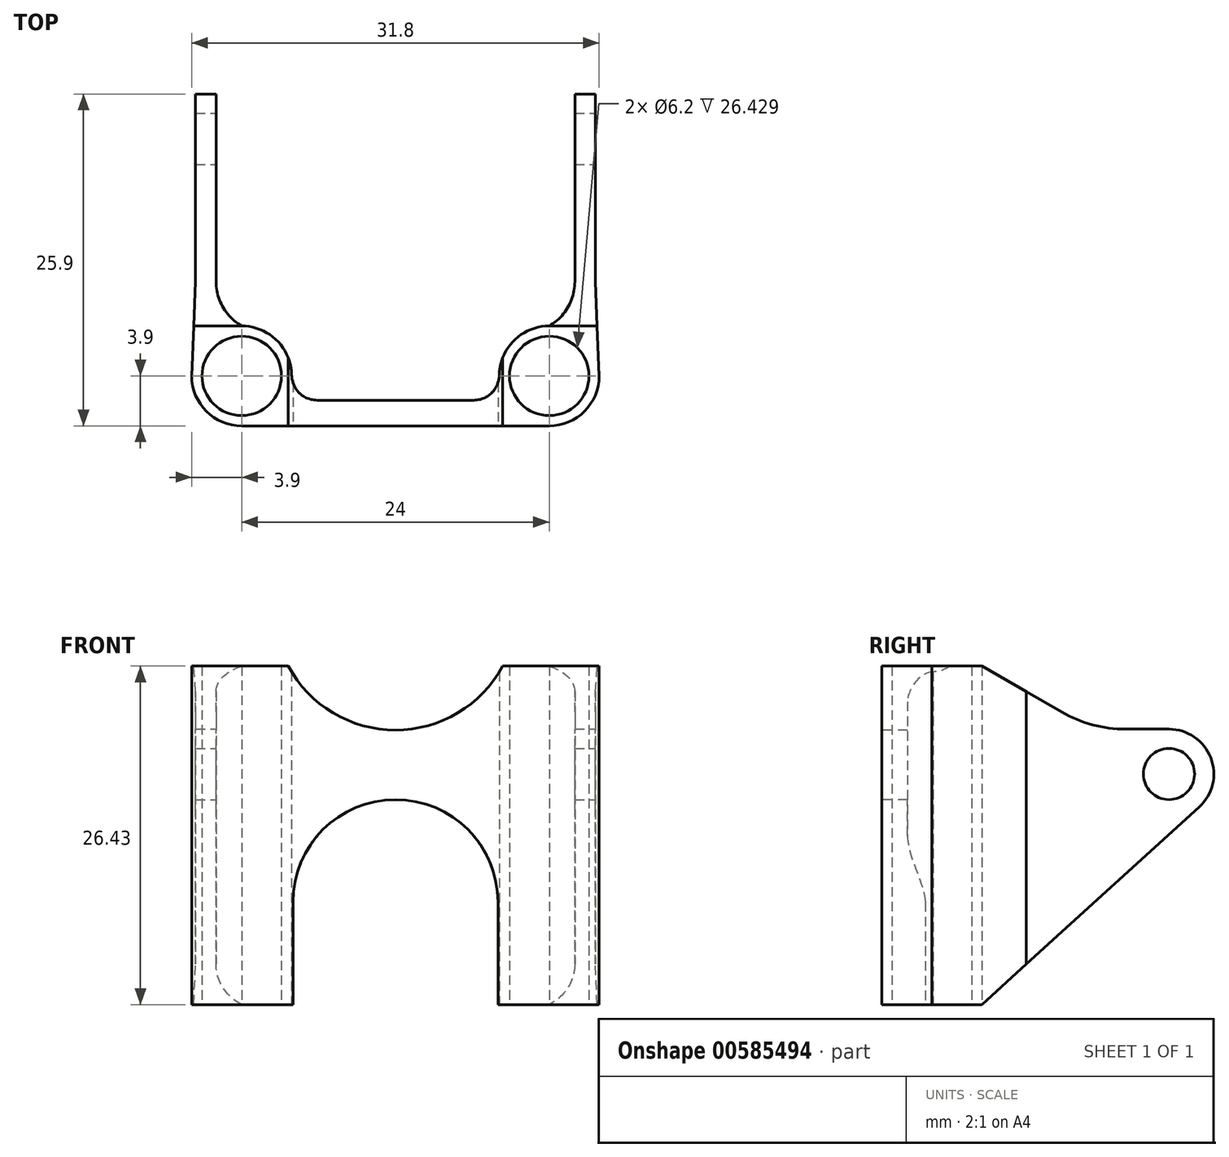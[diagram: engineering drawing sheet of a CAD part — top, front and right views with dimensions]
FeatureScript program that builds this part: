
annotation { "Feature Type Name" : "Feature", "Feature Type Description" : "" }
export const myFeature = defineFeature(function(context is Context, id is Id, definition is map)
    precondition{}
    {
        {
            var Q0;
            Q0=qCreatedBy(makeId("Top.planeOp"),FACE);
            var sketch = newSketch(context, id + "F0", { "sketchPlane" : qUnion([Q0])});
            skCircle(sketch, "E0", {"center": v(-24, 0) * mm, "radius": 3.1 * mm});
            skCircle(sketch, "E1", {"center": v(0, 0) * mm, "radius": 3.1 * mm});
            skLineSegment(sketch, "E2", {"start": v(3.6, 22) * mm, "end": v(2, 22) * mm});
            skLineSegment(sketch, "E3", {"start": v(2, 22) * mm, "end": v(2, 7.36) * mm});
            skLineSegment(sketch, "E4", {"start": v(-27.6, 22) * mm, "end": v(-26, 22) * mm});
            skLineSegment(sketch, "E5", {"start": v(-26, 22) * mm, "end": v(-26, 7.36) * mm});
            skArc(sketch, "E6.filletArc", {"start": v(-26, 7.36) * mm, "mid": v(-25.46, 5.36) * mm, "end": v(-24, 3.9) * mm});
            skArc(sketch, "E7.filletArc", {"start": v(0, 3.9) * mm, "mid": v(1.46, 5.36) * mm, "end": v(2, 7.36) * mm});
            skLineSegment(sketch, "E8", {"start": v(3.6, 22) * mm, "end": v(3.6, 7.36) * mm});
            skCircle(sketch, "E9", {"center": v(0, 0) * mm, "radius": 3.9 * mm});
            skPoint(sketch, "E10.startSnap0", {"position": v(1.46, 5.36) * mm});
            skCircle(sketch, "E11", {"center": v(-24, 0) * mm, "radius": 3.9 * mm});
            skLineSegment(sketch, "E12", {"start": v(-27.6, 22) * mm, "end": v(-27.6, 7.36) * mm});
            skLineSegment(sketch, "E13", {"start": v(0, 0) * mm, "end": v(3.9, 0) * mm, "construction": true});
            skLineSegment(sketch, "E14", {"start": v(-24, 0) * mm, "end": v(-24, 3.9) * mm, "construction": true});
            skLineSegment(sketch, "E15", {"start": v(0, 0) * mm, "end": v(0, 3.9) * mm, "construction": true});
            skLineSegment(sketch, "E16", {"start": v(-24, 0) * mm, "end": v(-27.9, 0) * mm, "construction": true});
            skLineSegment(sketch, "E17", {"start": v(-24, 0) * mm, "end": v(-24, -3.9) * mm, "construction": true});
            skLineSegment(sketch, "E18", {"start": v(0, 0) * mm, "end": v(0, -3.9) * mm, "construction": true});
            skLineSegment(sketch, "E19", {"start": v(0, -3.9) * mm, "end": v(-24, -3.9) * mm});
            skPoint(sketch, "E20", {"position": v(-12, -3.9) * mm});
            skLineSegment(sketch, "E21", {"start": v(-5.9, -1.9) * mm, "end": v(-18.1, -1.9) * mm});
            skLineSegment(sketch, "E22", {"start": v(3.6, 7.36) * mm, "end": v(3.9, 0) * mm});
            skLineSegment(sketch, "E23", {"start": v(-27.6, 7.36) * mm, "end": v(-27.9, 0) * mm});
            skLineSegment(sketch, "E24", {"start": v(0, 0) * mm, "end": v(-3.9, 0) * mm, "construction": true});
            skLineSegment(sketch, "E25", {"start": v(-24, 0) * mm, "end": v(-20.1, 0) * mm, "construction": true});
            skLineSegment(sketch, "E26", {"start": v(-20.1, 0.1) * mm, "end": v(-20.1, 0) * mm});
            skLineSegment(sketch, "E27", {"start": v(-3.9, 0.1) * mm, "end": v(-3.9, 0) * mm});
            skArc(sketch, "E28.filletArc", {"start": v(-5.9, -1.9) * mm, "mid": v(-4.49, -1.31) * mm, "end": v(-3.9, 0.1) * mm});
            skArc(sketch, "E29.filletArc", {"start": v(-20.1, 0.1) * mm, "mid": v(-19.51, -1.31) * mm, "end": v(-18.1, -1.9) * mm});
            skSolve(sketch);
        }
        {
            var Q0;
            Q0=makeQuery(id+"F0.imprint","IMPRINT",FACE,{"disambiguationData":[TD([[makeQuery(id+"F0.imprint","IMPRINT",EDGE,{"derivedFrom":sQuery(id+"F0.wireOp",EDGE,"E0")}),-1.0]])]});
            var Q1;
            Q1=makeQuery(id+"F0.imprint","IMPRINT",FACE,{"disambiguationData":[TD([[makeQuery(id+"F0.imprint","IMPRINT",EDGE,{"derivedFrom":sQuery(id+"F0.wireOp",EDGE,"E4")}),-1.0]])]});
            var Q2;
            {var subQ0=sQuery(id+"F0.wireOp",EDGE,"E19");Q2=makeQuery(id+"F0.imprint","IMPRINT",FACE,{"disambiguationData":[TD([[makeQuery(id+"F0.imprint","IMPRINT",EDGE,{"derivedFrom":subQ0}),-1.0]])]});}
            var Q3;
            Q3=makeQuery(id+"F0.imprint","IMPRINT",FACE,{"disambiguationData":[TD([[makeQuery(id+"F0.imprint","IMPRINT",EDGE,{"derivedFrom":sQuery(id+"F0.wireOp",EDGE,"E1")}),-1.0]])]});
            var Q4;
            Q4=makeQuery(id+"F0.imprint","IMPRINT",FACE,{"disambiguationData":[TD([[makeQuery(id+"F0.imprint","IMPRINT",EDGE,{"derivedFrom":sQuery(id+"F0.wireOp",EDGE,"E2")}),1.0]])]});
            extrude(context, id + "F1", {"entities" : qUnion([Q0, Q1, Q2, Q3, Q4]), "depth" : 35 * mm, "offsetDistance" : 25 * mm});
        }
        {
            var Q0;
            Q0=makeQuery(id+"F1.opExtrude","SWEPT_FACE",FACE,{"disambiguationData":[OSD([sQuery(id+"F0.wireOp",EDGE,"E8")])]});
            var sketch = newSketch(context, id + "F2", { "sketchPlane" : qUnion([Q0])});
            skPoint(sketch, "E30", {"position": v(18.5, 18) * mm});
            skCircle(sketch, "E31", {"center": v(18.5, 18) * mm, "radius": 2 * mm});
            skCircle(sketch, "E32", {"center": v(18.5, 18) * mm, "radius": 3.5 * mm});
            skLineSegment(sketch, "E33", {"start": v(18.5, 18) * mm, "end": v(-11.95, 18) * mm, "construction": true});
            skLineSegment(sketch, "E34", {"start": v(18.5, 18) * mm, "end": v(-7.48, 33) * mm, "construction": true});
            skPoint(sketch, "E35", {"position": v(-7.48, 33) * mm});
            skLineSegment(sketch, "E36", {"start": v(18.5, 21.5) * mm, "end": v(15.12, 21.5) * mm});
            skLineSegment(sketch, "E37", {"start": v(10.12, 22.84) * mm, "end": v(-4.4, 31.22) * mm});
            skPoint(sketch, "E38.visualSharp", {"position": v(12.44, 21.5) * mm});
            skArc(sketch, "E38.filletArc", {"start": v(10.12, 22.84) * mm, "mid": v(12.53, 21.84) * mm, "end": v(15.12, 21.5) * mm});
            skLineSegment(sketch, "E39", {"start": v(-4.4, 31.22) * mm, "end": v(-4.4, 42.85) * mm});
            skLineSegment(sketch, "E40", {"start": v(-4.4, 42.85) * mm, "end": v(29.67, 42.85) * mm});
            skLineSegment(sketch, "E41", {"start": v(29.67, 42.85) * mm, "end": v(29.67, 18) * mm});
            skLineSegment(sketch, "E42", {"start": v(18.5, 18) * mm, "end": v(22, 18) * mm, "construction": true});
            skLineSegment(sketch, "E43", {"start": v(29.67, 18) * mm, "end": v(22, 18) * mm});
            skPoint(sketch, "E44", {"position": v(3.9, 0) * mm});
            skLineSegment(sketch, "E45", {"start": v(3.9, 0) * mm, "end": v(20.85, 15.4) * mm});
            skLineSegment(sketch, "E46", {"start": v(3.9, 0) * mm, "end": v(22, 0) * mm});
            skSolve(sketch);
        }
        {
            var Q0;
            {var subQ6=sQuery(id+"F2.wireOp",EDGE,"E36");Q0=makeQuery(id+"F2.imprint","IMPRINT",FACE,{"disambiguationData":[TD([[makeQuery(id+"F2.imprint","IMPRINT",EDGE,{"derivedFrom":subQ6}),-1.0]])]});}
            var Q1;
            {var subQ0=sQuery(id+"F2.wireOp",EDGE,"E39");Q1=makeQuery(id+"F2.imprint","IMPRINT",FACE,{"disambiguationData":[TD([[makeQuery(id+"F2.imprint","IMPRINT",EDGE,{"derivedFrom":subQ0}),-1.0]])]});}
            var Q2;
            Q2=makeQuery(id+"F2.imprint","IMPRINT",FACE,{"disambiguationData":[TD([[makeQuery(id+"F2.imprint","IMPRINT",EDGE,{"derivedFrom":sQuery(id+"F2.wireOp",EDGE,"E31")}),1.0]])]});
            var Q3;
            {var subQ0=sQuery(id+"F2.wireOp",EDGE,"uojOCUMa-Bsdn-c8Zq-LXbt-Cjw3FCOuAA6H");Q3=makeQuery(id+"F2.imprint","IMPRINT",FACE,{"disambiguationData":[TD([[makeQuery(id+"F2.imprint","IMPRINT",EDGE,{"derivedFrom":subQ0}),-1.0]])]});}
            var Q4;
            {var subQ0=sQuery(id+"F0.wireOp",EDGE,"E8");var subQ1=makeQuery(id+"F1.opExtrude","CAP_EDGE",EDGE,{"disambiguationData":[OSD([subQ0])],"isStart":true});Q4=makeQuery(id+"F2.imprint","IMPRINT",FACE,{"disambiguationData":[TD([[makeQuery(id+"F2.imprint","IMPRINT",EDGE,{"derivedFrom":subQ1}),-1.0]])]});}
            var Q5;
            {var subQ0=sQuery(id+"F2.wireOp",EDGE,"E46");Q5=makeQuery(id+"F2.imprint","IMPRINT",FACE,{"disambiguationData":[TD([[makeQuery(id+"F2.imprint","IMPRINT",EDGE,{"derivedFrom":subQ0}),1.0]])]});}
            var Q6;
            {var subQ4=sQuery(id+"F2.wireOp",EDGE,"E32");var subQ8=sQuery(id+"F2.wireOp",EDGE,"E45");var subQ9=makeQuery(id+"F2.imprint","INTERSECT",VERTEX,{"derivedFrom":[subQ4,subQ8]});Q6=makeQuery(id+"F2.imprint","IMPRINT",FACE,{"disambiguationData":[TD([[makeQuery(id+"F2.imprint","IMPRINT",EDGE,{"disambiguationData":[TD([[subQ9,1.0]])],"derivedFrom":subQ8}),-1.0]])]});}
            extrude(context, id + "F3", {"entities" : qUnion([Q0, Q1, Q2, Q3, Q4, Q5, Q6]), "operationType" : NewBodyOperationType.REMOVE, "endBound" : BoundingType.THROUGH_ALL, "oppositeDirection" : true, "depth" : 25 * mm, "offsetDistance" : 25 * mm, "hasSecondDirection" : true, "secondDirectionBound" : SecondDirectionBoundingType.THROUGH_ALL, "secondDirectionOppositeDirection" : false, "secondDirectionDepth" : 25 * mm});
        }
        {
            var Q0;
            Q0=makeQuery(id+"F1.opExtrude","SWEPT_FACE",FACE,{"disambiguationData":[OSD([sQuery(id+"F0.wireOp",EDGE,"E19")])]});
            var sketch = newSketch(context, id + "F4", { "sketchPlane" : qUnion([Q0])});
            skCircle(sketch, "E47", {"center": v(-12, 8) * mm, "radius": 8 * mm});
            skCircle(sketch, "E48", {"center": v(-12, 30.93) * mm, "radius": 9.5 * mm});
            skLineSegment(sketch, "E49", {"start": v(-12, 8) * mm, "end": v(-4, 8) * mm, "construction": true});
            skLineSegment(sketch, "E50", {"start": v(-4, 8) * mm, "end": v(-4, 0) * mm});
            skLineSegment(sketch, "E51", {"start": v(-12, 8) * mm, "end": v(-20, 8) * mm, "construction": true});
            skLineSegment(sketch, "E52", {"start": v(-20, 8) * mm, "end": v(-20, 0) * mm});
            skPoint(sketch, "E53", {"position": v(0, 26.43) * mm});
            skLineSegment(sketch, "E54", {"start": v(0, 26.43) * mm, "end": v(8.47, 26.43) * mm});
            skLineSegment(sketch, "E55", {"start": v(8.47, 26.43) * mm, "end": v(8.47, 34.59) * mm});
            skLineSegment(sketch, "E56", {"start": v(8.47, 34.59) * mm, "end": v(-31.34, 34.59) * mm});
            skLineSegment(sketch, "E57", {"start": v(-31.34, 34.59) * mm, "end": v(-31.34, 26.43) * mm});
            skLineSegment(sketch, "E58", {"start": v(-31.34, 26.43) * mm, "end": v(0, 26.43) * mm});
            skSolve(sketch);
        }
        {
            var Q0;
            {var subQ0=sQuery(id+"F4.wireOp",EDGE,"E48");var subQ1=makeQuery(id+"F3.boolean.opBoolean","INTERSECT",EDGE,{"derivedFrom":[makeQuery(id+"F1.opExtrude","SWEPT_FACE",FACE,{"disambiguationData":[OSD([sQuery(id+"F0.wireOp",EDGE,"SeFjCfSd-k32o-aJPD-k4J2-v6AQV1DPfuQB.bottom")])]}),makeQuery(id+"F3.opExtrude","SWEPT_FACE",FACE,{"disambiguationData":[OSD([sQuery(id+"F2.wireOp",EDGE,"E37")])]})]});var subQ2=makeQuery(id+"F4.imprint","INTERSECT",VERTEX,{"disambiguationData":[OD(0.0)],"derivedFrom":[subQ1,subQ0]});Q0=makeQuery(id+"F4.imprint","IMPRINT",FACE,{"disambiguationData":[TD([[makeQuery(id+"F4.imprint","IMPRINT",EDGE,{"disambiguationData":[TD([[subQ2,1.0]])],"derivedFrom":subQ0}),1.0]])]});}
            var Q1;
            {var subQ0=sQuery(id+"F4.wireOp",EDGE,"E47");var subQ1=makeQuery(id+"F1.opExtrude","CAP_EDGE",EDGE,{"disambiguationData":[OSD([sQuery(id+"F0.wireOp",EDGE,"SeFjCfSd-k32o-aJPD-k4J2-v6AQV1DPfuQB.bottom")])],"isStart":true});var subQ2=makeQuery(id+"F4.imprint","INTERSECT",VERTEX,{"disambiguationData":[OD(0.0)],"derivedFrom":[subQ1,subQ0]});Q1=makeQuery(id+"F4.imprint","IMPRINT",FACE,{"disambiguationData":[TD([[makeQuery(id+"F4.imprint","IMPRINT",EDGE,{"disambiguationData":[TD([[subQ2,-1.0]])],"derivedFrom":subQ0}),1.0]])]});}
            var Q2;
            {var subQ0=sQuery(id+"F4.wireOp",EDGE,"E50");Q2=makeQuery(id+"F4.imprint","IMPRINT",FACE,{"disambiguationData":[TD([[makeQuery(id+"F4.imprint","IMPRINT",EDGE,{"derivedFrom":subQ0}),-1.0]])]});}
            var Q3;
            {var subQ0=sQuery(id+"F4.wireOp",EDGE,"E52");Q3=makeQuery(id+"F4.imprint","IMPRINT",FACE,{"disambiguationData":[TD([[makeQuery(id+"F4.imprint","IMPRINT",EDGE,{"derivedFrom":subQ0}),1.0]])]});}
            var Q4;
            {var subQ0=sQuery(id+"F4.wireOp",EDGE,"E58");var subQ1=sQuery(id+"F4.wireOp",EDGE,"E48");var subQ2=makeQuery(id+"F4.imprint","INTERSECT",VERTEX,{"disambiguationData":[OD(0.0)],"derivedFrom":[subQ1,subQ0]});Q4=makeQuery(id+"F4.imprint","IMPRINT",FACE,{"disambiguationData":[TD([[makeQuery(id+"F4.imprint","IMPRINT",EDGE,{"disambiguationData":[TD([[subQ2,-1.0]])],"derivedFrom":subQ1}),1.0]])]});}
            var Q5;
            {var subQ1=sQuery(id+"F4.wireOp",EDGE,"E57");Q5=makeQuery(id+"F4.imprint","IMPRINT",FACE,{"disambiguationData":[TD([[makeQuery(id+"F4.imprint","IMPRINT",EDGE,{"derivedFrom":subQ1}),1.0]])]});}
            var Q6;
            {var subQ1=sQuery(id+"F4.wireOp",EDGE,"E54");Q6=makeQuery(id+"F4.imprint","IMPRINT",FACE,{"disambiguationData":[TD([[makeQuery(id+"F4.imprint","IMPRINT",EDGE,{"derivedFrom":subQ1}),1.0]])]});}
            var Q7;
            {var subQ0=sQuery(id+"F4.wireOp",EDGE,"E58");var subQ1=sQuery(id+"F4.wireOp",EDGE,"E48");var subQ2=makeQuery(id+"F4.imprint","INTERSECT",VERTEX,{"disambiguationData":[OD(1.0)],"derivedFrom":[subQ1,subQ0]});Q7=makeQuery(id+"F4.imprint","IMPRINT",FACE,{"disambiguationData":[TD([[makeQuery(id+"F4.imprint","IMPRINT",EDGE,{"disambiguationData":[TD([[subQ2,-1.0]])],"derivedFrom":subQ1}),-1.0]])]});}
            var Q8;
            {var subQ0=sQuery(id+"F4.wireOp",EDGE,"E58");var subQ1=sQuery(id+"F4.wireOp",EDGE,"E48");var subQ2=makeQuery(id+"F4.imprint","INTERSECT",VERTEX,{"disambiguationData":[OD(0.0)],"derivedFrom":[subQ1,subQ0]});Q8=makeQuery(id+"F4.imprint","IMPRINT",FACE,{"disambiguationData":[TD([[makeQuery(id+"F4.imprint","IMPRINT",EDGE,{"disambiguationData":[TD([[subQ2,1.0]])],"derivedFrom":subQ1}),-1.0]])]});}
            var Q9;
            {var subQ0=sQuery(id+"F4.wireOp",EDGE,"E58");var subQ1=sQuery(id+"F4.wireOp",EDGE,"E48");var subQ2=makeQuery(id+"F4.imprint","INTERSECT",VERTEX,{"disambiguationData":[OD(0.0)],"derivedFrom":[subQ1,subQ0]});Q9=makeQuery(id+"F4.imprint","IMPRINT",FACE,{"disambiguationData":[TD([[makeQuery(id+"F4.imprint","IMPRINT",EDGE,{"disambiguationData":[TD([[subQ2,1.0]])],"derivedFrom":subQ1}),1.0]])]});}
            extrude(context, id + "F5", {"entities" : qUnion([Q0, Q1, Q2, Q3, Q4, Q5, Q6, Q7, Q8, Q9]), "operationType" : NewBodyOperationType.REMOVE, "endBound" : BoundingType.THROUGH_ALL, "oppositeDirection" : true, "depth" : 25 * mm, "offsetDistance" : 25 * mm});
        }
    });
